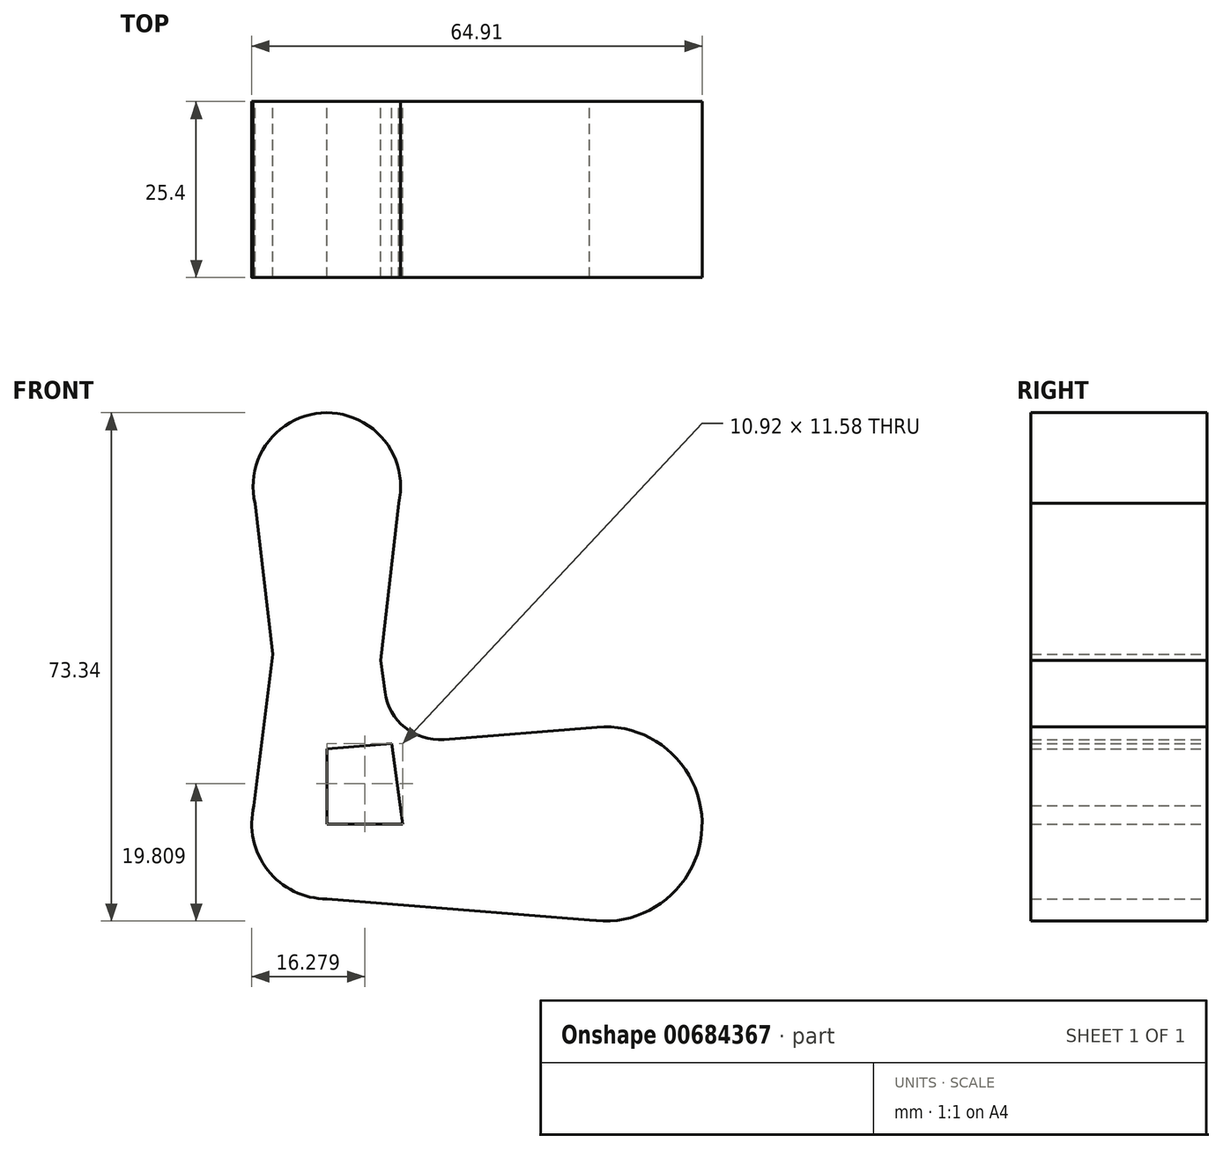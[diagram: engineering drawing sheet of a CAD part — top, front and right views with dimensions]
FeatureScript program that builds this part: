
annotation { "Feature Type Name" : "Feature", "Feature Type Description" : "" }
export const myFeature = defineFeature(function(context is Context, id is Id, definition is map)
    precondition{}
    {
        {
            var Q0;
            Q0=qCreatedBy(makeId("Front.planeOp"),FACE);
            var sketch = newSketch(context, id + "F0", { "sketchPlane" : qUnion([Q0])});
            skCircle(sketch, "E0", {"center": v(0, 0) * mm, "radius": 10.82 * mm});
            skCircle(sketch, "E1", {"center": v(40.08, 0) * mm, "radius": 14.02 * mm});
            skCircle(sketch, "E2", {"center": v(0, 24.48) * mm, "radius": 7.81 * mm});
            skCircle(sketch, "E3", {"center": v(0, 48.68) * mm, "radius": 10.64 * mm});
            skLineSegment(sketch, "E4", {"start": v(0, 0) * mm, "end": v(40.08, 0) * mm});
            skLineSegment(sketch, "E5", {"start": v(0, 0) * mm, "end": v(0, 24.48) * mm});
            skLineSegment(sketch, "E6", {"start": v(0, 24.48) * mm, "end": v(0, 48.68) * mm});
            skLineSegment(sketch, "E7", {"start": v(0, 48.68) * mm, "end": v(0, -40.8) * mm});
            skLineSegment(sketch, "E8", {"start": v(-10.64, 48.68) * mm, "end": v(-7.81, 24.48) * mm});
            skLineSegment(sketch, "E9", {"start": v(-7.81, 24.48) * mm, "end": v(-10.64, 48.68) * mm});
            skLineSegment(sketch, "E10", {"start": v(10.64, 48.68) * mm, "end": v(7.76, 23.6) * mm});
            skLineSegment(sketch, "E11", {"start": v(7.76, 23.6) * mm, "end": v(10.64, 48.68) * mm});
            skLineSegment(sketch, "E12", {"start": v(-7.81, 24.48) * mm, "end": v(-10.82, 0) * mm});
            skLineSegment(sketch, "E13", {"start": v(-10.82, 0) * mm, "end": v(-7.81, 24.48) * mm});
            skLineSegment(sketch, "E14", {"start": v(7.76, 23.6) * mm, "end": v(10.92, 0) * mm});
            skLineSegment(sketch, "E15", {"start": v(8.37, 19.06) * mm, "end": v(7.76, 23.6) * mm});
            skLineSegment(sketch, "E16", {"start": v(0, -10.82) * mm, "end": v(40.08, -14.02) * mm});
            skLineSegment(sketch, "E17", {"start": v(40.08, -14.02) * mm, "end": v(0, -10.82) * mm});
            skLineSegment(sketch, "E18", {"start": v(16.89, 12.19) * mm, "end": v(40.08, 14.06) * mm});
            skLineSegment(sketch, "E19", {"start": v(40.08, 14.06) * mm, "end": v(0, 10.82) * mm});
            skPoint(sketch, "E20.newPointA", {"position": v(0, 10.82) * mm});
            skArc(sketch, "E20.filletArc", {"start": v(8.37, 19.06) * mm, "mid": v(11.26, 13.92) * mm, "end": v(16.89, 12.19) * mm});
            skSolve(sketch);
        }
        {
            var Q0;
            Q0 = qSketchRegion(id + "F0", true);
            extrude(context, id + "F1", {"entities" : qUnion([Q0]), "depth" : 25.4 * mm, "offsetDistance" : 25.4 * mm});
        }
    });
